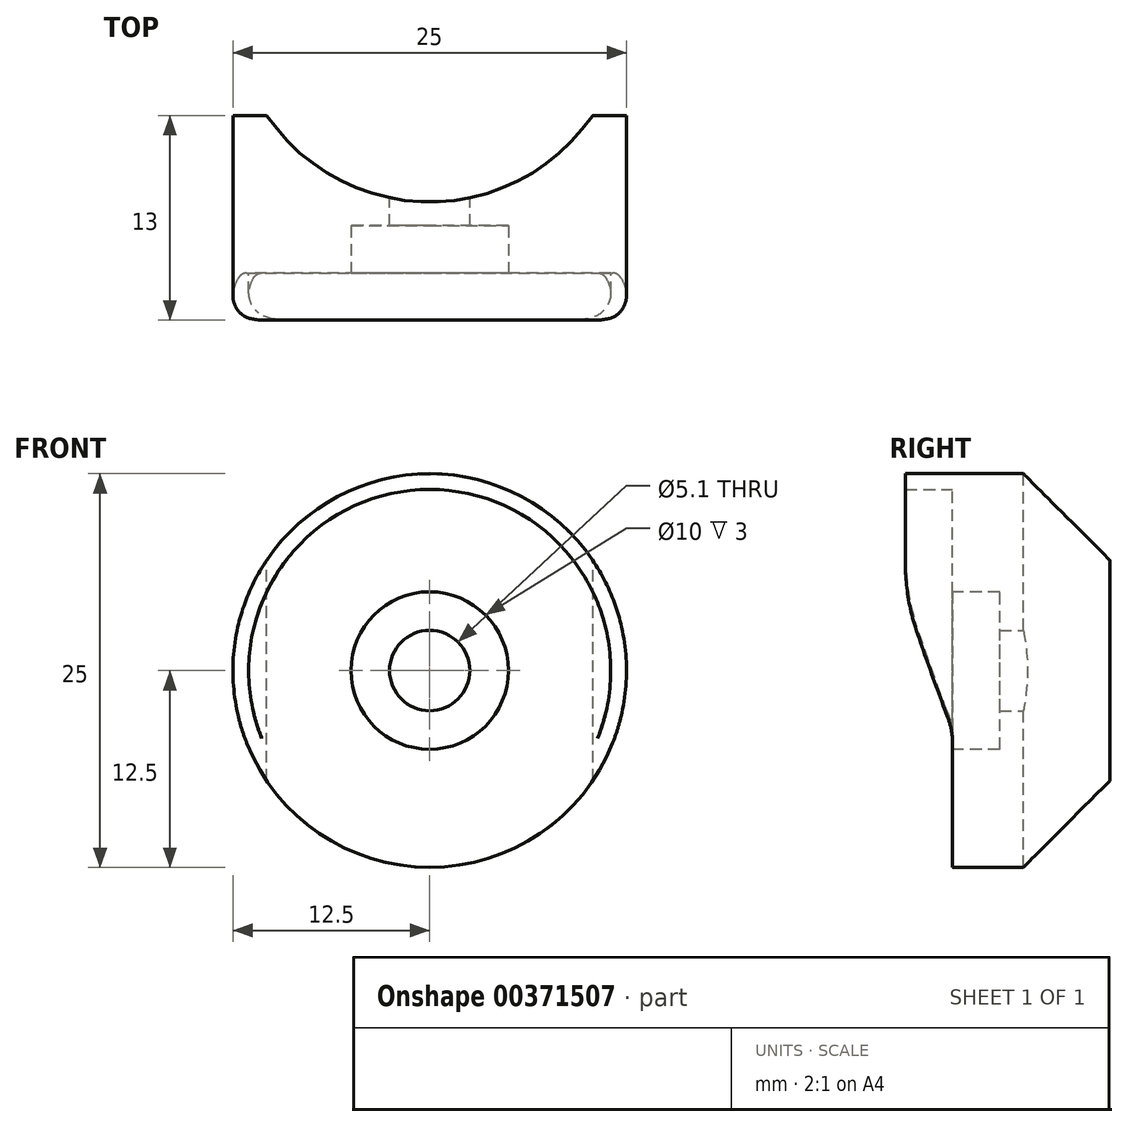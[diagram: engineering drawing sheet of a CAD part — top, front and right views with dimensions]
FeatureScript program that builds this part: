
annotation { "Feature Type Name" : "Feature", "Feature Type Description" : "" }
export const myFeature = defineFeature(function(context is Context, id is Id, definition is map)
    precondition{}
    {
        {
            var Q0;
            Q0=qCreatedBy(makeId("Front.planeOp"),FACE);
            var sketch = newSketch(context, id + "F0", { "sketchPlane" : qUnion([Q0])});
            skCircle(sketch, "E0", {"center": v(0, 0) * mm, "radius": 12.5 * mm});
            skSolve(sketch);
        }
        {
            var Q0;
            Q0=makeQuery(id+"F0.imprint","IMPRINT",FACE,{"disambiguationData":[TD([[makeQuery(id+"F0.imprint","IMPRINT",EDGE,{"derivedFrom":sQuery(id+"F0.wireOp",EDGE,"E0")}),1.0]])]});
            extrude(context, id + "F1", {"entities" : qUnion([Q0]), "endBound" : BoundingType.SYMMETRIC, "depth" : 10 * mm, "offsetDistance" : 25 * mm});
        }
        {
            var Q0;
            Q0=makeQuery(id+"F1.opExtrude","CAP_FACE",FACE,{"disambiguationData":[OSD([sQuery(id+"F0.wireOp",EDGE,"E0")])],"isStart":false});
            var sketch = newSketch(context, id + "F2", { "sketchPlane" : qUnion([Q0])});
            skCircle(sketch, "E1", {"center": v(0, 0) * mm, "radius": 11.5 * mm});
            skSolve(sketch);
        }
        {
            var Q0;
            Q0=qCreatedBy(makeId("Top.planeOp"),FACE);
            var sketch = newSketch(context, id + "F3", { "sketchPlane" : qUnion([Q0])});
            skCircle(sketch, "E2", {"center": v(0, 12) * mm, "radius": 12.5 * mm});
            skSolve(sketch);
        }
        {
            var Q0;
            Q0=makeQuery(id+"F3.imprint","IMPRINT",FACE,{"disambiguationData":[TD([[makeQuery(id+"F3.imprint","IMPRINT",EDGE,{"derivedFrom":sQuery(id+"F3.wireOp",EDGE,"E2")}),1.0]])]});
            extrude(context, id + "F4", {"entities" : qUnion([Q0]), "operationType" : NewBodyOperationType.REMOVE, "endBound" : BoundingType.SYMMETRIC, "oppositeDirection" : true, "depth" : 25 * mm, "offsetDistance" : 25 * mm});
        }
        {
            var Q0;
            Q0=makeQuery(id+"F2.imprint","IMPRINT",FACE,{"disambiguationData":[TD([[makeQuery(id+"F2.imprint","IMPRINT",EDGE,{"derivedFrom":sQuery(id+"F2.wireOp",EDGE,"E1")}),1.0]])]});
            var sketch = newSketch(context, id + "F5", { "sketchPlane" : qUnion([Q0])});
            skLineSegment(sketch, "E3", {"start": v(0, 0) * mm, "end": v(12.6, -3.97) * mm, "construction": true});
            skLineSegment(sketch, "E4", {"start": v(0, 14.86) * mm, "end": v(0, -15.43) * mm, "construction": true});
            skLineSegment(sketch, "E5.MirrorCS", {"start": v(0, 0) * mm, "end": v(-12.6, -3.97) * mm, "construction": true});
            skArc(sketch, "E6", {"start": v(-10.97, -3.46) * mm, "mid": v(0, 11.5) * mm, "end": v(10.97, -3.46) * mm});
            skArc(sketch, "E7", {"start": v(-11.92, -3.76) * mm, "mid": v(0, 12.5) * mm, "end": v(11.92, -3.76) * mm});
            skLineSegment(sketch, "E8", {"start": v(10.97, -3.46) * mm, "end": v(11.92, -3.76) * mm, "construction": true});
            skLineSegment(sketch, "E9", {"start": v(-10.97, -3.46) * mm, "end": v(-11.92, -3.76) * mm});
            skLineSegment(sketch, "E10", {"start": v(10.97, -3.46) * mm, "end": v(11.92, -3.76) * mm});
            skSolve(sketch);
        }
        {
            var Q0;
            Q0=makeQuery(id+"F5.imprint","IMPRINT",FACE,{"disambiguationData":[TD([[makeQuery(id+"F5.imprint","IMPRINT",EDGE,{"derivedFrom":sQuery(id+"F5.wireOp",EDGE,"E6")}),-1.0]])]});
            extrude(context, id + "F6", {"entities" : qUnion([Q0]), "operationType" : NewBodyOperationType.ADD, "depth" : 3 * mm, "offsetDistance" : 25 * mm});
        }
        {
            var Q0;
            Q0=makeQuery(id+"F2.imprint","IMPRINT",FACE,{"disambiguationData":[TD([[makeQuery(id+"F2.imprint","IMPRINT",EDGE,{"derivedFrom":sQuery(id+"F2.wireOp",EDGE,"E1")}),1.0]])]});
            var sketch = newSketch(context, id + "F7", { "sketchPlane" : qUnion([Q0])});
            skCircle(sketch, "E11", {"center": v(0, 0) * mm, "radius": 2.55 * mm});
            skSolve(sketch);
        }
        {
            var Q0;
            Q0=makeQuery(id+"F7.imprint","IMPRINT",FACE,{"disambiguationData":[TD([[makeQuery(id+"F7.imprint","IMPRINT",EDGE,{"derivedFrom":sQuery(id+"F7.wireOp",EDGE,"E11")}),1.0]])]});
            var Q1;
            Q1=sQuery(id+"F7.wireOp",EDGE,"E11");
            extrude(context, id + "F8", {"entities" : qUnion([Q0]), "operationType" : NewBodyOperationType.REMOVE, "surfaceEntities" : qUnion([Q1]), "endBound" : BoundingType.SYMMETRIC, "depth" : 25 * mm, "offsetDistance" : 25 * mm});
        }
        {
            var Q0;
            Q0=makeQuery(id+"F2.imprint","IMPRINT",FACE,{"disambiguationData":[TD([[makeQuery(id+"F2.imprint","IMPRINT",EDGE,{"derivedFrom":sQuery(id+"F2.wireOp",EDGE,"E1")}),1.0]])]});
            var sketch = newSketch(context, id + "F9", { "sketchPlane" : qUnion([Q0])});
            skCircle(sketch, "E12", {"center": v(0, 0) * mm, "radius": 5 * mm});
            skSolve(sketch);
        }
        {
            var Q0;
            Q0=makeQuery(id+"F9.imprint","IMPRINT",FACE,{"disambiguationData":[TD([[makeQuery(id+"F9.imprint","IMPRINT",EDGE,{"derivedFrom":sQuery(id+"F9.wireOp",EDGE,"E12")}),1.0]])]});
            extrude(context, id + "F10", {"entities" : qUnion([Q0]), "operationType" : NewBodyOperationType.REMOVE, "oppositeDirection" : true, "depth" : 3 * mm, "offsetDistance" : 25 * mm});
        }
        {
            var Q0;
            Q0=makeQuery(id+"F6.opExtrude","CAP_EDGE",EDGE,{"disambiguationData":[OSD([sQuery(id+"F5.wireOp",EDGE,"E9")])],"isStart":false});
            var Q1;
            Q1=makeQuery(id+"F6.opExtrude","CAP_EDGE",EDGE,{"disambiguationData":[OSD([sQuery(id+"F5.wireOp",EDGE,"E10")])],"isStart":false});
            chamfer(context, id + "F11", {"entities" : qUnion([Q0, Q1]), "chamferType" : ChamferType.TWO_OFFSETS, "width1" : 3 * mm, "oppositeDirection" : false, "width2" : 8 * mm, "tangentPropagation" : true});
        }
        {
            var Q0;
            {var subQ0=sQuery(id+"F5.wireOp",EDGE,"E9");Q0=makeQuery(id+"F11.opChamfer","BLEND_EDGE",EDGE,{"blendedFrom":[makeQuery(id+"F6.opExtrude","CAP_EDGE",EDGE,{"disambiguationData":[OSD([subQ0])],"isStart":false}),makeQuery(id+"F6.opExtrude","CAP_FACE",FACE,{"disambiguationData":[OSD([sQuery(id+"F5.wireOp",EDGE,"E6"),sQuery(id+"F5.wireOp",EDGE,"E7"),subQ0,sQuery(id+"F5.wireOp",EDGE,"E10")])],"isStart":false})],"blendedInto":[makeQuery(id+"F6.opExtrude","CAP_FACE",FACE,{"disambiguationData":[OSD([sQuery(id+"F5.wireOp",EDGE,"E6"),sQuery(id+"F5.wireOp",EDGE,"E7"),subQ0,sQuery(id+"F5.wireOp",EDGE,"E10")])],"isStart":false})]});}
            var Q1;
            {var subQ0=sQuery(id+"F5.wireOp",EDGE,"E10");Q1=makeQuery(id+"F11.opChamfer","BLEND_EDGE",EDGE,{"blendedFrom":[makeQuery(id+"F6.opExtrude","CAP_EDGE",EDGE,{"disambiguationData":[OSD([subQ0])],"isStart":false}),makeQuery(id+"F6.opExtrude","CAP_FACE",FACE,{"disambiguationData":[OSD([sQuery(id+"F5.wireOp",EDGE,"E6"),sQuery(id+"F5.wireOp",EDGE,"E7"),sQuery(id+"F5.wireOp",EDGE,"E9"),subQ0])],"isStart":false})],"blendedInto":[makeQuery(id+"F6.opExtrude","CAP_FACE",FACE,{"disambiguationData":[OSD([sQuery(id+"F5.wireOp",EDGE,"E6"),sQuery(id+"F5.wireOp",EDGE,"E7"),sQuery(id+"F5.wireOp",EDGE,"E9"),subQ0])],"isStart":false})]});}
            fillet(context, id + "F12", {"entities" : qUnion([Q0, Q1]), "tangentPropagation" : true, "radius" : 10 * mm, "defaultsChanged" : true, "vertexSettings" : [], "allowEdgeOverflow" : false});
        }
        {
            var Q0;
            Q0=makeQuery(id+"F11.opChamfer","BLEND_EDGE",EDGE,{"blendedFrom":[makeQuery(id+"F6.opExtrude","CAP_EDGE",EDGE,{"disambiguationData":[OSD([sQuery(id+"F5.wireOp",EDGE,"E9")])],"isStart":false}),makeQuery(id+"F1.opExtrude","CAP_FACE",FACE,{"disambiguationData":[OSD([sQuery(id+"F0.wireOp",EDGE,"E0")])],"isStart":false})],"blendedInto":[makeQuery(id+"F1.opExtrude","CAP_FACE",FACE,{"disambiguationData":[OSD([sQuery(id+"F0.wireOp",EDGE,"E0")])],"isStart":false})]});
            var Q1;
            Q1=makeQuery(id+"F11.opChamfer","BLEND_EDGE",EDGE,{"blendedFrom":[makeQuery(id+"F6.opExtrude","CAP_EDGE",EDGE,{"disambiguationData":[OSD([sQuery(id+"F5.wireOp",EDGE,"E10")])],"isStart":false}),makeQuery(id+"F1.opExtrude","CAP_FACE",FACE,{"disambiguationData":[OSD([sQuery(id+"F0.wireOp",EDGE,"E0")])],"isStart":false})],"blendedInto":[makeQuery(id+"F1.opExtrude","CAP_FACE",FACE,{"disambiguationData":[OSD([sQuery(id+"F0.wireOp",EDGE,"E0")])],"isStart":false})]});
            fillet(context, id + "F13", {"entities" : qUnion([Q0, Q1]), "tangentPropagation" : true, "radius" : 5 * mm, "defaultsChanged" : false, "vertexSettings" : [], "allowEdgeOverflow" : false});
        }
    });
